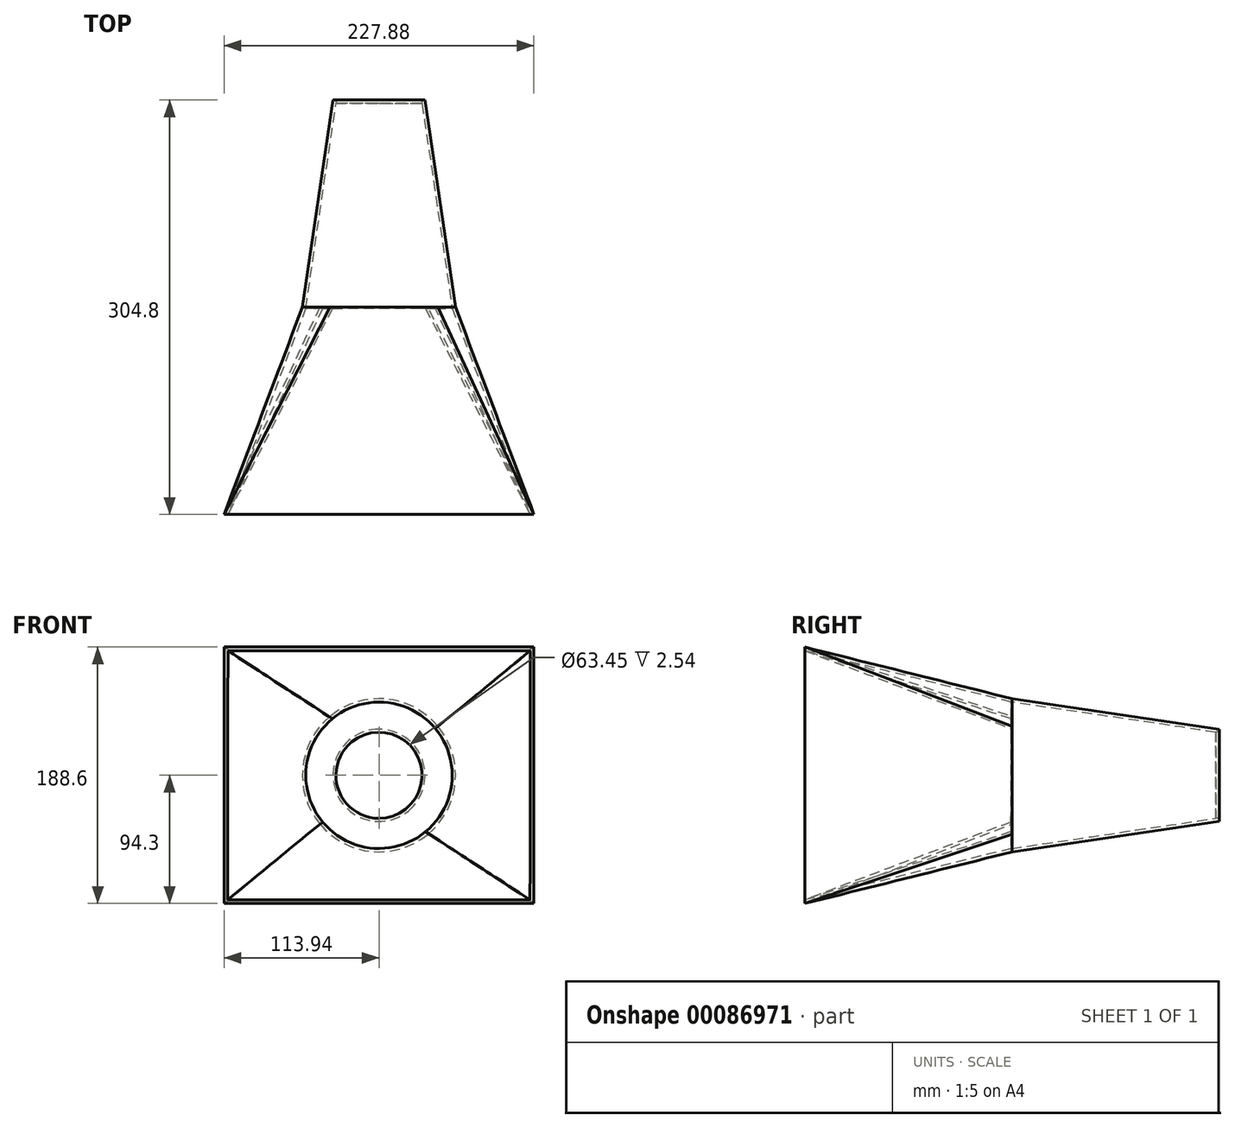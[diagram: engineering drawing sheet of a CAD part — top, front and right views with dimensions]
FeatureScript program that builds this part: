
annotation { "Feature Type Name" : "Feature", "Feature Type Description" : "" }
export const myFeature = defineFeature(function(context is Context, id is Id, definition is map)
    precondition{}
    {
        {
            var Q0;
            Q0=qCreatedBy(makeId("Front.planeOp"),FACE);
            var sketch = newSketch(context, id + "F0", { "sketchPlane" : qUnion([Q0])});
            skCircle(sketch, "E0", {"center": v(0, 0) * mm, "radius": 56.32 * mm});
            skSolve(sketch);
        }
        {
            var Q0;
            Q0=qCreatedBy(makeId("Front.planeOp"),FACE);
            cPlane(context, id + "F1", {"entities" : qUnion([Q0]), "cplaneType" : CPlaneType.OFFSET, "offset" : 152.4 * mm, "width" : 152.4 * mm, "height" : 152.4 * mm});
        }
        {
            var Q0;
            Q0=qCreatedBy(id+"F1.planeOp",FACE);
            var sketch = newSketch(context, id + "F2", { "sketchPlane" : qUnion([Q0])});
            skLineSegment(sketch, "E1.bottom", {"start": v(113.94, 94.3) * mm, "end": v(-113.94, 94.3) * mm});
            skLineSegment(sketch, "E1.top", {"start": v(113.94, -94.3) * mm, "end": v(-113.94, -94.3) * mm});
            skLineSegment(sketch, "E1.left", {"start": v(113.94, 94.3) * mm, "end": v(113.94, -94.3) * mm});
            skLineSegment(sketch, "E1.right", {"start": v(-113.94, 94.3) * mm, "end": v(-113.94, -94.3) * mm});
            skPoint(sketch, "E1.middle", {"position": v(0, 0) * mm});
            skSolve(sketch);
        }
        {
            var Q0;
            Q0=makeQuery(id+"F2.imprint","IMPRINT",FACE,{"disambiguationData":[TD([[makeQuery(id+"F2.imprint","IMPRINT",EDGE,{"derivedFrom":sQuery(id+"F2.wireOp",EDGE,"E1.bottom")}),1.0]])]});
            var Q1;
            Q1=makeQuery(id+"F0.imprint","IMPRINT",FACE,{"disambiguationData":[TD([[makeQuery(id+"F0.imprint","IMPRINT",EDGE,{"derivedFrom":sQuery(id+"F0.wireOp",EDGE,"E0")}),1.0]])]});
            loft(context, id + "F3", {"sheetProfilesArray" : [{ "sheetProfileEntities" : qUnion([Q0]) }, { "sheetProfileEntities" : qUnion([Q1]) }]});
        }
        {
            var Q0;
            Q0=makeQuery(id+"F3.opLoft","CAP_FACE",FACE,{"disambiguationData":[OSD([makeQuery(id+"F0.imprint","IMPRINT",FACE,{"disambiguationData":[TD([[makeQuery(id+"F0.imprint","IMPRINT",EDGE,{"derivedFrom":sQuery(id+"F0.wireOp",EDGE,"E0")}),1.0]])]})])],"isStart":true});
            cPlane(context, id + "F4", {"entities" : qUnion([Q0]), "cplaneType" : CPlaneType.OFFSET, "offset" : 152.4 * mm, "width" : 152.4 * mm, "height" : 152.4 * mm});
        }
        {
            var Q0;
            Q0=makeQuery(id+"F3.opLoft","CAP_FACE",FACE,{"disambiguationData":[OSD([makeQuery(id+"F0.imprint","IMPRINT",FACE,{"disambiguationData":[TD([[makeQuery(id+"F0.imprint","IMPRINT",EDGE,{"derivedFrom":sQuery(id+"F0.wireOp",EDGE,"E0")}),1.0]])]})])],"isStart":true});
            var sketch = newSketch(context, id + "F5", { "sketchPlane" : qUnion([Q0])});
            skCircle(sketch, "E2", {"center": v(0, 0) * mm, "radius": 56.32 * mm});
            skSolve(sketch);
        }
        {
            var Q0;
            Q0=qCreatedBy(id+"F4.planeOp",FACE);
            var sketch = newSketch(context, id + "F6", { "sketchPlane" : qUnion([Q0])});
            skCircle(sketch, "E3", {"center": v(0, 0) * mm, "radius": 33.87 * mm});
            skSolve(sketch);
        }
        {
            var Q0;
            {var subQ0=sQuery(id+"F5.wireOp",EDGE,"E2");var subQ1=makeQuery(id+"F5.imprint","IMPRINT",VERTEX,{"disambiguationData":[OD(2.0)],"derivedFrom":subQ0});Q0=makeQuery(id+"F5.imprint","IMPRINT",FACE,{"disambiguationData":[TD([[makeQuery(id+"F5.imprint","IMPRINT",EDGE,{"disambiguationData":[TD([[subQ1,-1.0]])],"derivedFrom":subQ0}),1.0]])]});}
            var Q1;
            Q1=makeQuery(id+"F6.imprint","IMPRINT",FACE,{"disambiguationData":[TD([[makeQuery(id+"F6.imprint","IMPRINT",EDGE,{"derivedFrom":sQuery(id+"F6.wireOp",EDGE,"E3")}),1.0]])]});
            loft(context, id + "F7", {"operationType" : NewBodyOperationType.ADD, "sheetProfilesArray" : [{ "sheetProfileEntities" : qUnion([Q0]) }, { "sheetProfileEntities" : qUnion([Q1]) }]});
        }
        {
            var Q0;
            Q0=makeQuery(id+"F3.opLoft","CAP_FACE",FACE,{"disambiguationData":[OSD([makeQuery(id+"F2.imprint","IMPRINT",FACE,{"disambiguationData":[TD([[makeQuery(id+"F2.imprint","IMPRINT",EDGE,{"derivedFrom":sQuery(id+"F2.wireOp",EDGE,"E1.bottom")}),1.0]])]})])],"isStart":true});
            shell(context, id + "F8", {"entities" : qUnion([Q0]), "thickness" : 2.54 * mm});
        }
        {
            var Q0;
            Q0=makeQuery(id+"F8.opShell","OFFSET_FACE",FACE,{"disambiguationData":[OSD([makeQuery(id+"F6.imprint","IMPRINT",FACE,{"disambiguationData":[TD([[makeQuery(id+"F6.imprint","IMPRINT",EDGE,{"derivedFrom":sQuery(id+"F6.wireOp",EDGE,"E3")}),1.0]])]})])]});
            var sketch = newSketch(context, id + "F9", { "sketchPlane" : qUnion([Q0])});
            skCircle(sketch, "E4", {"center": v(0, 0) * mm, "radius": 31.72 * mm});
            skSolve(sketch);
        }
        {
            var Q0;
            Q0 = qSketchRegion(id + "F9", true);
            extrude(context, id + "F10", {"entities" : qUnion([Q0]), "operationType" : NewBodyOperationType.REMOVE, "oppositeDirection" : true, "depth" : 126.16 * mm});
        }
    });
